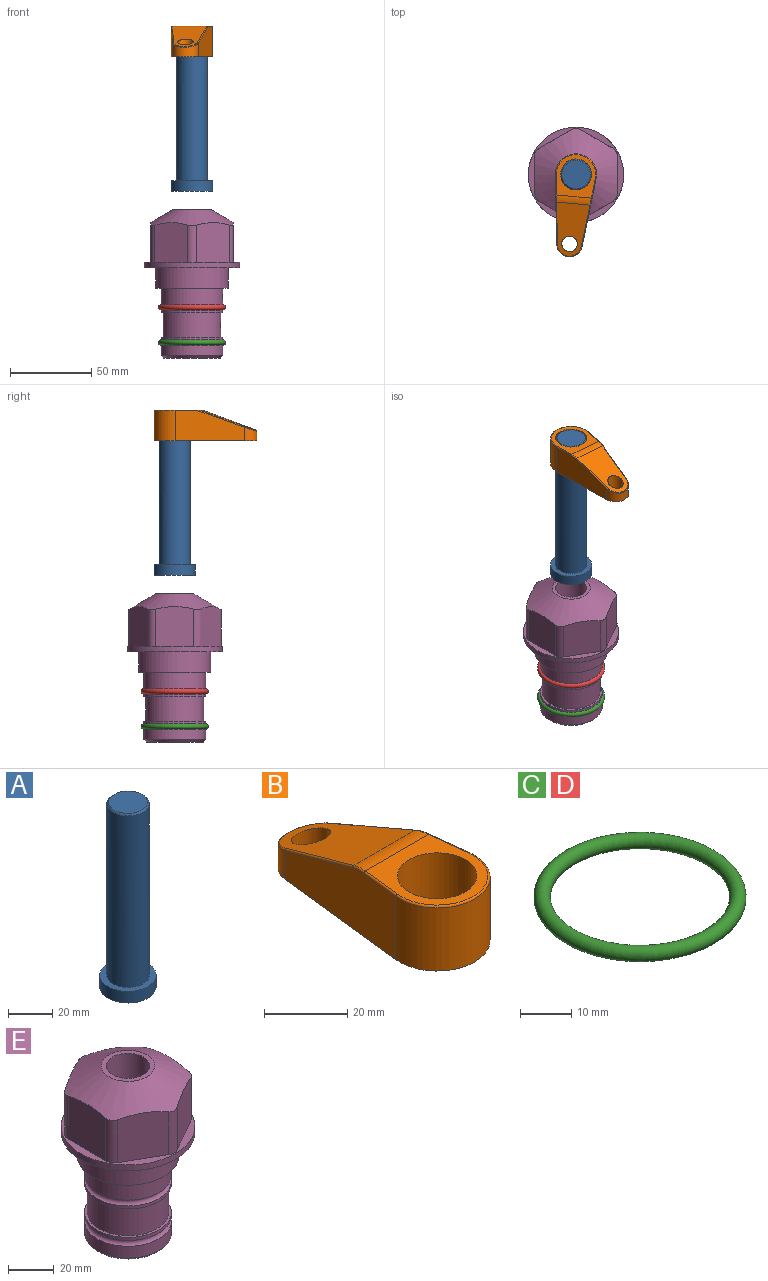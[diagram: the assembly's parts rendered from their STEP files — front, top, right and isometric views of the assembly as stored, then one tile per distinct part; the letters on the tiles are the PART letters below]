
ASSEMBLY  parts=5 mates=3
PART A: 6 faces, bbox 25.4x25.4x101.6 mm
  f0: plane 17.46x17.46mm, normal (0,0,1), area 239.5mm2, adj f5
  f1: plane 25.4x25.4mm, normal (0,0,-1), area 506.7mm2, adj f2
  f2: cylinder r=12.7mm len=25.4mm, axis (0,0,1), area 506.7mm2, adj f1,f3
  f3: plane 25.4x25.4mm, normal (0,0,1), area 221.7mm2, adj f2,f4
  f4: cylinder r=9.53mm len=94.46mm, axis (0,0,1), area 5653mm2, adj f3,f5
  f5: cone r=8.73mm half-angle=45deg, axis (0,0,-1), area 64.4mm2, adj f0,f4
PART B: 44 faces, bbox 27.5x64.5x19.1 mm
  f0: plane 2.3x0.95mm, normal (0,0,-1), area 1mm2, adj f25,f30,f34
  f1: plane 63.5x25.4mm, normal (0,0,-1), area 561.7mm2, adj f2,f3,f4,f5,f6,f7,f19,f20
  f2: cylinder r=12.7mm len=25.4mm, axis (0,0,-1), area 792.2mm2, adj f1,f3,f5,f13
  f3: plane 42.33x18.54mm, normal (0.99,0.11,0), area 647mm2, adj f1,f2,f4,f11,f12,f14
  f4: cylinder r=7.94mm len=15.78mm, axis (0,0,-1), area 158.6mm2, adj f1,f3,f5,f16
  f5: plane 42.33x18.54mm, normal (-0.99,0.11,0), area 647mm2, adj f1,f2,f4,f15,f17,f18
  f6: cylinder r=9.53mm len=19.05mm, axis (0,0,-1), area 1140.1mm2, adj f1,f8
  f7: cylinder r=4.76mm len=10.98mm, axis (0,0,-1), area 276.1mm2, adj f1,f9
  f8: plane 25.83x24.38mm, normal (0,0,1), area 262.2mm2, adj f6,f10,f11,f13,f15
  f9: plane 32.49x20.55mm, normal (0,0.34,0.94), area 489.9mm2, adj f7,f10,f14,f16,f18
  f10: cylinder r=12.7mm len=21.49mm, axis (-1,0,0), area 93.2mm2, adj f8,f9,f12,f17
  f11: cylinder r=0.51mm len=12.34mm, axis (0.11,-0.99,0), area 9.9mm2, adj f3,f8,f12,f13
  f12: bspline ~7.62x1.64mm, area 3.5mm2, adj f3,f10,f11,f14
  f13: torus R=12.19mm, axis (0,0,1), area 33.6mm2, adj f2,f8,f11,f15
  f14: cylinder r=0.51mm len=26.01mm, axis (0.1,-0.93,0.34), area 21.6mm2, adj f3,f9,f12,f16
  f15: cylinder r=0.51mm len=12.34mm, axis (0.11,0.99,0), area 9.9mm2, adj f5,f8,f13,f17
  f16: bspline ~15.78x7.05mm, area 15.7mm2, adj f4,f9,f14,f18
  f17: bspline ~7.62x1.64mm, area 3.5mm2, adj f5,f10,f15,f18
  f18: cylinder r=0.51mm len=26.01mm, axis (0.1,0.93,-0.34), area 21.6mm2, adj f5,f9,f16,f17
  f19: plane 21.6x14.29mm, normal (-0.99,-0.11,0), area 242.6mm2, adj f1,f26,f28,f34,f36,f38
  f20: plane 21.6x14.29mm, normal (0.99,-0.11,0), area 242.6mm2, adj f1,f27,f29,f37,f39,f41
  f21: cylinder r=12.7mm len=14.29mm, axis (0,0,-1), area 173.2mm2, adj f1,f26,f27,f30,f31,f33
  f22: cylinder r=7.94mm len=7.63mm, axis (0,0,-1), area 53.8mm2, adj f1,f28,f29,f42
  f23: plane 2.3x0.95mm, normal (0,0,-1), area 1mm2, adj f25,f33,f37
  f24: plane 17.94x12.32mm, normal (0,-0.34,-0.94), area 191.2mm2, adj f25,f38,f41,f42
  f25: cylinder r=9.53mm len=12.93mm, axis (-1,0,0), area 37.5mm2, adj f0,f23,f24,f31,f36,f39
  f26: cylinder r=1.59mm len=14.29mm, axis (0,0,-1), area 49mm2, adj f1,f19,f21,f32
  f27: cylinder r=1.59mm len=14.29mm, axis (0,0,-1), area 49mm2, adj f1,f20,f21,f35
  f28: cylinder r=1.59mm len=7.28mm, axis (0,0,-1), area 22.1mm2, adj f1,f19,f22,f40
  f29: cylinder r=1.59mm len=7.28mm, axis (0,0,-1), area 22.1mm2, adj f1,f20,f22,f43
  f30: torus R=14.29mm, axis (0,0,1), area 5.8mm2, adj f0,f21,f31,f32
  f31: bspline ~11.06x2.73mm, area 20.8mm2, adj f21,f25,f30,f33
  f32: sphere r=1.59mm, area 5.4mm2, adj f26,f30,f34
  f33: torus R=14.29mm, axis (0,0,1), area 5.8mm2, adj f21,f23,f31,f35
  f34: cylinder r=1.59mm len=1.68mm, axis (-0.11,0.99,0), area 2.4mm2, adj f0,f19,f32,f36
  f35: sphere r=1.59mm, area 5.4mm2, adj f27,f33,f37
  f36: bspline ~5.82x2.33mm, area 7.7mm2, adj f19,f25,f34,f38
  f37: cylinder r=1.59mm len=1.68mm, axis (0.11,0.99,0), area 2.4mm2, adj f20,f23,f35,f39
  f38: cylinder r=1.59mm len=18.33mm, axis (0.1,-0.93,0.34), area 46.7mm2, adj f19,f24,f36,f40
  f39: bspline ~5.82x2.33mm, area 7.7mm2, adj f20,f25,f37,f41
  f40: sphere r=1.59mm, area 3.6mm2, adj f28,f38,f42
  f41: cylinder r=1.59mm len=18.33mm, axis (0.1,0.93,-0.34), area 46.7mm2, adj f20,f24,f39,f43
  f42: bspline ~8.31x1.84mm, area 15.3mm2, adj f22,f24,f40,f43
  f43: sphere r=1.59mm, area 3.6mm2, adj f29,f41,f42
PART C: 1 faces, bbox 44.7x44.7x3.2 mm
  f0: torus R=19.05mm, axis (0,0,1), area 1193.9mm2
PART D: same geometry as C
PART E: 36 faces, bbox 58.7x58.7x91.2 mm
  f0: cylinder r=17.78mm len=35.56mm, axis (0,0,1), area 1670.8mm2, adj f23,f24,f31
  f1: cylinder r=19.05mm len=38.1mm, axis (0,0,1), area 1191.9mm2, adj f26,f27,f30
  f2: plane 58.66x58.66mm, normal (0,0,-1), area 1150.6mm2, adj f3,f28
  f3: cylinder r=29.33mm len=58.66mm, axis (0,0,-1), area 585.1mm2, adj f2,f4
  f4: plane 58.66x58.66mm, normal (0,0,1), area 475.9mm2, adj f3,f5,f6,f7,f8,f9,f10,f11
  f5: plane 24.5x20.32mm, normal (-0.5,0.87,0), area 562.8mm2, adj f4,f15,f16,f17
  f6: plane 24.5x20.32mm, normal (0.5,0.87,0), area 562.8mm2, adj f4,f14,f15,f17
  f7: plane 24.5x23.48mm, normal (1,0,0), area 562.8mm2, adj f4,f13,f14,f17
  f8: plane 24.5x20.32mm, normal (0.5,-0.87,0), area 562.8mm2, adj f4,f12,f13,f17
  f9: plane 24.5x20.32mm, normal (-0.5,-0.87,0), area 562.8mm2, adj f4,f11,f12,f17
  f10: plane 24.5x23.48mm, normal (-1,0,0), area 562.8mm2, adj f4,f11,f16,f17
  f11: cylinder r=5.08mm len=23.01mm, axis (0,0,-1), area 121.2mm2, adj f4,f9,f10,f17
  f12: cylinder r=5.08mm len=23.01mm, axis (0,0,-1), area 121.2mm2, adj f4,f8,f9,f17
  f13: cylinder r=5.08mm len=23.01mm, axis (0,0,-1), area 121.2mm2, adj f4,f7,f8,f17
  f14: cylinder r=5.08mm len=23.01mm, axis (0,0,-1), area 121.2mm2, adj f4,f6,f7,f17
  f15: cylinder r=5.08mm len=23.01mm, axis (0,0,-1), area 121.2mm2, adj f4,f5,f6,f17
  f16: cylinder r=5.08mm len=23.01mm, axis (0,0,-1), area 121.2mm2, adj f4,f5,f10,f17
  f17: cone r=11.73mm half-angle=60deg, axis (0,0,-1), area 2071.8mm2, adj f5,f6,f7,f8,f9,f10,f11,f12
  f18: plane 23.46x23.46mm, normal (0,0,1), area 147.4mm2, adj f17,f35
  f19: plane 34.93x34.93mm, normal (0,0,-1), area 958mm2, adj f29
  f20: cylinder r=19.05mm len=38.1mm, axis (0,0,1), area 760.1mm2, adj f21,f29
  f21: torus R=19.05mm, axis (0,0,1), area 565.3mm2, adj f20,f22
  f22: cylinder r=19.05mm len=38.1mm, axis (0,0,1), area 190mm2, adj f21,f23
  f23: plane 38.1x38.1mm, normal (0,0,1), area 146.9mm2, adj f0,f22
  f24: plane 38.1x38.1mm, normal (0,0,-1), area 146.9mm2, adj f0,f25
  f25: cylinder r=19.05mm len=38.1mm, axis (0,0,1), area 190mm2, adj f24,f26
  f26: torus R=19.05mm, axis (0,0,1), area 565.3mm2, adj f1,f25
  f27: plane 44.45x44.45mm, normal (0,0,-1), area 411.7mm2, adj f1,f28
  f28: cylinder r=22.23mm len=44.45mm, axis (0,0,1), area 1773.5mm2, adj f2,f27
  f29: cone r=19.05mm half-angle=45deg, axis (0,0,1), area 257.5mm2, adj f19,f20
  f30: cylinder r=3.17mm len=6.75mm, axis (-1,0,0), area 128mm2, adj f1,f33
  f31: cylinder r=3.17mm len=6.35mm, axis (-1,0,0), area 102.5mm2, adj f0,f33
  f32: plane 25.4x25.4mm, normal (0,0,1), area 506.7mm2, adj f33
  f33: cylinder r=12.7mm len=66.42mm, axis (0,0,-1), area 5236.2mm2, adj f30,f31,f32,f34
  f34: cone r=9.53mm half-angle=30deg, axis (0,0,-1), area 443.4mm2, adj f33,f35
  f35: cylinder r=9.53mm len=19.05mm, axis (0,0,-1), area 849mm2, adj f18,f34
PLACE A rot(axis=(0,0,-1),95.3deg) t=(0,0,74.98)mm
PLACE B rot(axis=(0,0,1),174.7deg) t=(0,0,129.59)mm
PLACE C t=(0,0,-21.59)mm
PLACE D at identity
PLACE E at identity fixed
MATE fastened C.f0 <-> E.f0  axis (0,0,1) through (0,0,-46.1)mm
MATE cylindrical A.f2 <-> E.f0  axis (0,0,1) through (0,0,100.62)mm
MATE fastened B.f2 <-> A.f2  axis (0,0,1) through (0,0,148.64)mm
